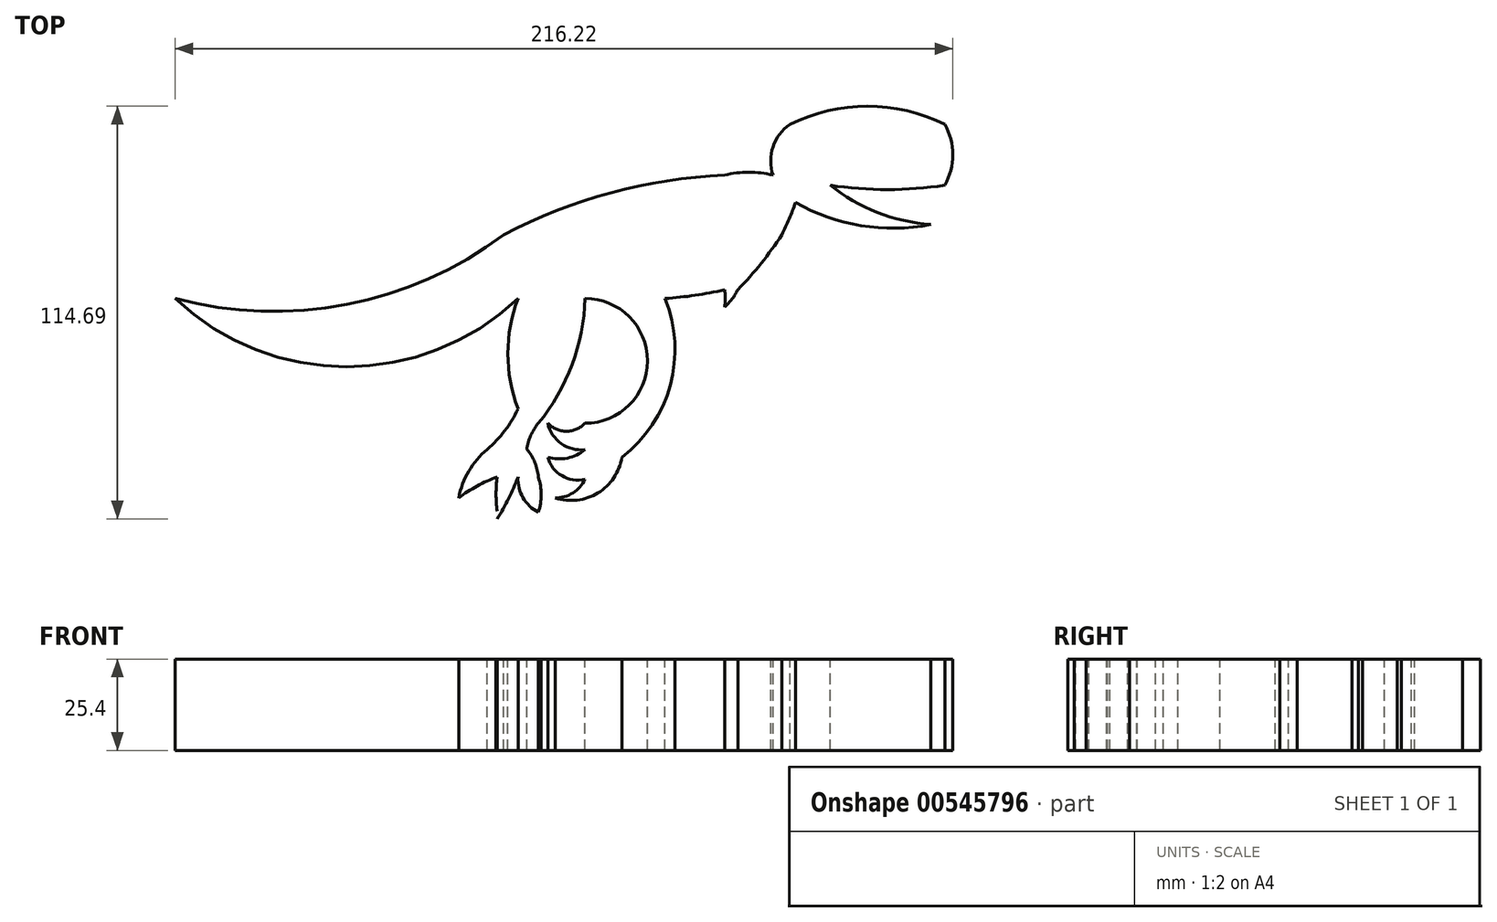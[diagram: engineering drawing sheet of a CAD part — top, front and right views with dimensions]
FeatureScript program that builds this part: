
annotation { "Feature Type Name" : "Feature", "Feature Type Description" : "" }
export const myFeature = defineFeature(function(context is Context, id is Id, definition is map)
    precondition{}
    {
        {
            var Q0;
            Q0=qCreatedBy(makeId("Top.planeOp"),FACE);
            var sketch = newSketch(context, id + "F0", { "sketchPlane" : qUnion([Q0])});
            skArc(sketch, "E0", {"start": v(-124, -17.73) * mm, "mid": v(-76.26, -19.4) * mm, "end": v(-32.6, 0) * mm});
            skArc(sketch, "E1", {"start": v(-124, -17.73) * mm, "mid": v(-76.32, -36.72) * mm, "end": v(-28.64, -17.73) * mm});
            skArc(sketch, "E2", {"start": v(28.76, 16.53) * mm, "mid": v(-2.84, 11.68) * mm, "end": v(-32.6, 0) * mm});
            skArc(sketch, "E3", {"start": v(-28.64, -17.73) * mm, "mid": v(-31.49, -33.1) * mm, "end": v(-28.64, -48.45) * mm});
            skArc(sketch, "E4", {"start": v(-37.19, -59.75) * mm, "mid": v(-32.35, -54.53) * mm, "end": v(-28.64, -48.45) * mm});
            skArc(sketch, "E5", {"start": v(-37.19, -59.75) * mm, "mid": v(-42.36, -65.76) * mm, "end": v(-45.13, -73.19) * mm});
            skArc(sketch, "E6", {"start": v(-34.44, -67.39) * mm, "mid": v(-40.02, -69.86) * mm, "end": v(-45.13, -73.19) * mm});
            skArc(sketch, "E7", {"start": v(-34.44, -67.39) * mm, "mid": v(-34.76, -72.12) * mm, "end": v(-34.44, -76.85) * mm});
            skArc(sketch, "E8", {"start": v(-34.44, -78.99) * mm, "mid": v(-31.25, -73.33) * mm, "end": v(-28.64, -67.39) * mm});
            skArc(sketch, "E9", {"start": v(-28.64, -67.39) * mm, "mid": v(-27.28, -73.13) * mm, "end": v(-23, -77.2) * mm});
            skArc(sketch, "E10", {"start": v(-23, -77.2) * mm, "mid": v(-22.23, -72.3) * mm, "end": v(-23, -67.39) * mm});
            skArc(sketch, "E11", {"start": v(-23, -67.39) * mm, "mid": v(-23.97, -63.3) * mm, "end": v(-26.2, -59.75) * mm});
            skArc(sketch, "E12", {"start": v(-23, -52.42) * mm, "mid": v(-25.15, -55.85) * mm, "end": v(-26.2, -59.75) * mm});
            skArc(sketch, "E13", {"start": v(-23, -52.42) * mm, "mid": v(-13.63, -36.16) * mm, "end": v(-10.01, -17.73) * mm});
            skArc(sketch, "E14", {"start": v(-10.01, -52.42) * mm, "mid": v(7.33, -35.08) * mm, "end": v(-10.01, -17.73) * mm});
            skArc(sketch, "E15", {"start": v(-20.4, -52.42) * mm, "mid": v(-15.2, -54.66) * mm, "end": v(-10.01, -52.42) * mm});
            skArc(sketch, "E16", {"start": v(-20.4, -52.42) * mm, "mid": v(-16.62, -58.1) * mm, "end": v(-10.01, -59.75) * mm});
            skArc(sketch, "E17", {"start": v(-20.4, -61.89) * mm, "mid": v(-14.93, -62.12) * mm, "end": v(-10.01, -59.75) * mm});
            skArc(sketch, "E18", {"start": v(-20.4, -61.89) * mm, "mid": v(-16.44, -67.05) * mm, "end": v(-10.01, -67.98) * mm});
            skArc(sketch, "E19", {"start": v(-18.32, -73.19) * mm, "mid": v(-13.4, -71.8) * mm, "end": v(-10.01, -67.98) * mm});
            skArc(sketch, "E20", {"start": v(-18.32, -73.19) * mm, "mid": v(-6.44, -71.82) * mm, "end": v(0.22, -61.89) * mm});
            skArc(sketch, "E21", {"start": v(0.22, -61.89) * mm, "mid": v(13.66, -41.83) * mm, "end": v(12.22, -17.73) * mm});
            skArc(sketch, "E22", {"start": v(12.22, -17.73) * mm, "mid": v(20.54, -16.86) * mm, "end": v(28.76, -15.33) * mm});
            skArc(sketch, "E23", {"start": v(28.76, -20.13) * mm, "mid": v(28.98, -17.73) * mm, "end": v(28.76, -15.33) * mm});
            skArc(sketch, "E24", {"start": v(28.76, -20.13) * mm, "mid": v(30.86, -17.9) * mm, "end": v(32.45, -15.27) * mm});
            skArc(sketch, "E25", {"start": v(32.45, -15.27) * mm, "mid": v(38.95, -7.95) * mm, "end": v(44.67, 0) * mm});
            skArc(sketch, "E26", {"start": v(42.22, 16.53) * mm, "mid": v(35.5, 17.4) * mm, "end": v(28.76, 16.53) * mm});
            skArc(sketch, "E27", {"start": v(46.94, 30.7) * mm, "mid": v(42.21, 24.4) * mm, "end": v(42.22, 16.53) * mm});
            skArc(sketch, "E28", {"start": v(90.02, 30.7) * mm, "mid": v(68.48, 35.7) * mm, "end": v(46.94, 30.7) * mm});
            skArc(sketch, "E29", {"start": v(90.02, 13.74) * mm, "mid": v(92.2, 22.23) * mm, "end": v(90.02, 30.7) * mm});
            skArc(sketch, "E30", {"start": v(58.1, 13.74) * mm, "mid": v(74.06, 12.54) * mm, "end": v(90.02, 13.74) * mm});
            skArc(sketch, "E31", {"start": v(58.1, 13.74) * mm, "mid": v(71.25, 6.18) * mm, "end": v(86.03, 2.84) * mm});
            skArc(sketch, "E32", {"start": v(44.67, 0) * mm, "mid": v(46.73, 4.41) * mm, "end": v(48.47, 8.97) * mm});
            skArc(sketch, "E33", {"start": v(48.47, 8.97) * mm, "mid": v(66.7, 2.5) * mm, "end": v(86.03, 2.84) * mm});
            skSolve(sketch);
        }
        {
            var Q0;
            Q0 = qConstructionFilter(qBodyType(qCreatedBy(id + "F0" ,EDGE), BodyType.WIRE), ConstructionObject.NO);
            extrude(context, id + "F1", {"bodyType" : ToolBodyType.SURFACE, "surfaceEntities" : qUnion([Q0]), "endBound" : BoundingType.SYMMETRIC, "depth" : 25.4 * mm, "offsetDistance" : 25.4 * mm});
        }
    });
